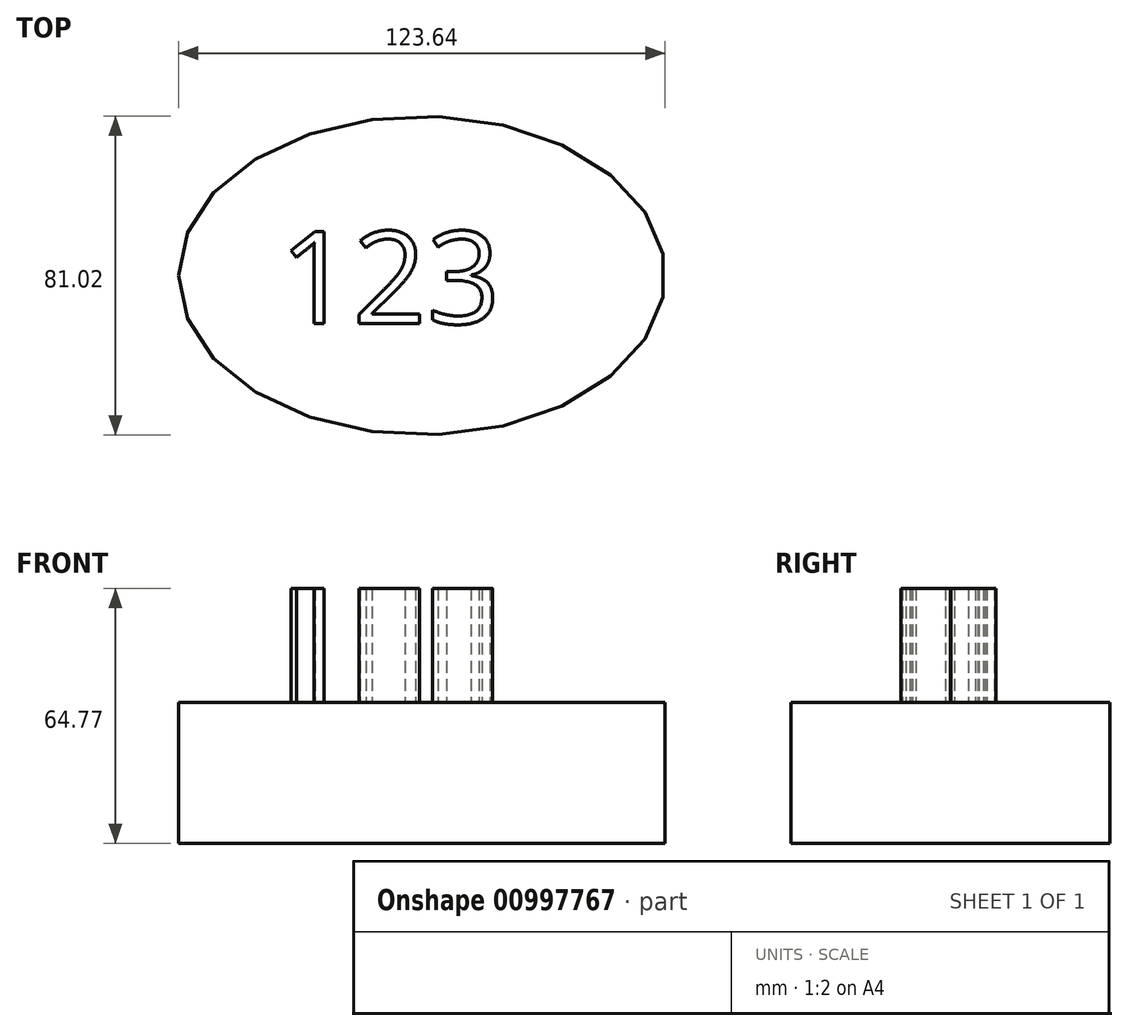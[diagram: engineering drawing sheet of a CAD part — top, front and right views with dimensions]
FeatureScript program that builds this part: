
annotation { "Feature Type Name" : "Feature", "Feature Type Description" : "" }
export const myFeature = defineFeature(function(context is Context, id is Id, definition is map)
    precondition{}
    {
        {
            var Q0;
            Q0=qCreatedBy(makeId("Top.planeOp"),FACE);
            var sketch = newSketch(context, id + "F0", { "sketchPlane" : qUnion([Q0])});
            skEllipse(sketch, "E0", {"center": v(0, 0) * mm, "majorRadius": 61.82 * mm, "minorRadius": 40.5 * mm, "majorAxis": v(-1, 0)});
            skSolve(sketch);
        }
        {
            var Q0;
            Q0 = qSketchRegion(id + "F0", true);
            extrude(context, id + "F1", {"entities" : qUnion([Q0]), "depth" : 35.81 * mm, "offsetDistance" : 25.4 * mm});
        }
        {
            var Q0;
            Q0=makeQuery(id+"F1.opExtrude","CAP_FACE",FACE,{"disambiguationData":[OSD([sQuery(id+"F0.wireOp",EDGE,"E0")])],"isStart":false});
            var sketch = newSketch(context, id + "F2", { "sketchPlane" : qUnion([Q0])});
            skText(sketch, "E1", { "text": "123\n", "fontName": "OpenSans-Regular.ttf"});
            const initialGuessF2  = {"E1": [-0.03624, -0.01221, 1, 0, 0.0236]};
            skSetInitialGuess(sketch, initialGuessF2);
            skSolve(sketch);
        }
        {
            var Q0;
            Q0 = qSketchRegion(id + "F2", true);
            extrude(context, id + "F3", {"entities" : qUnion([Q0]), "depth" : 28.96 * mm, "offsetDistance" : 25.4 * mm});
        }
    });
